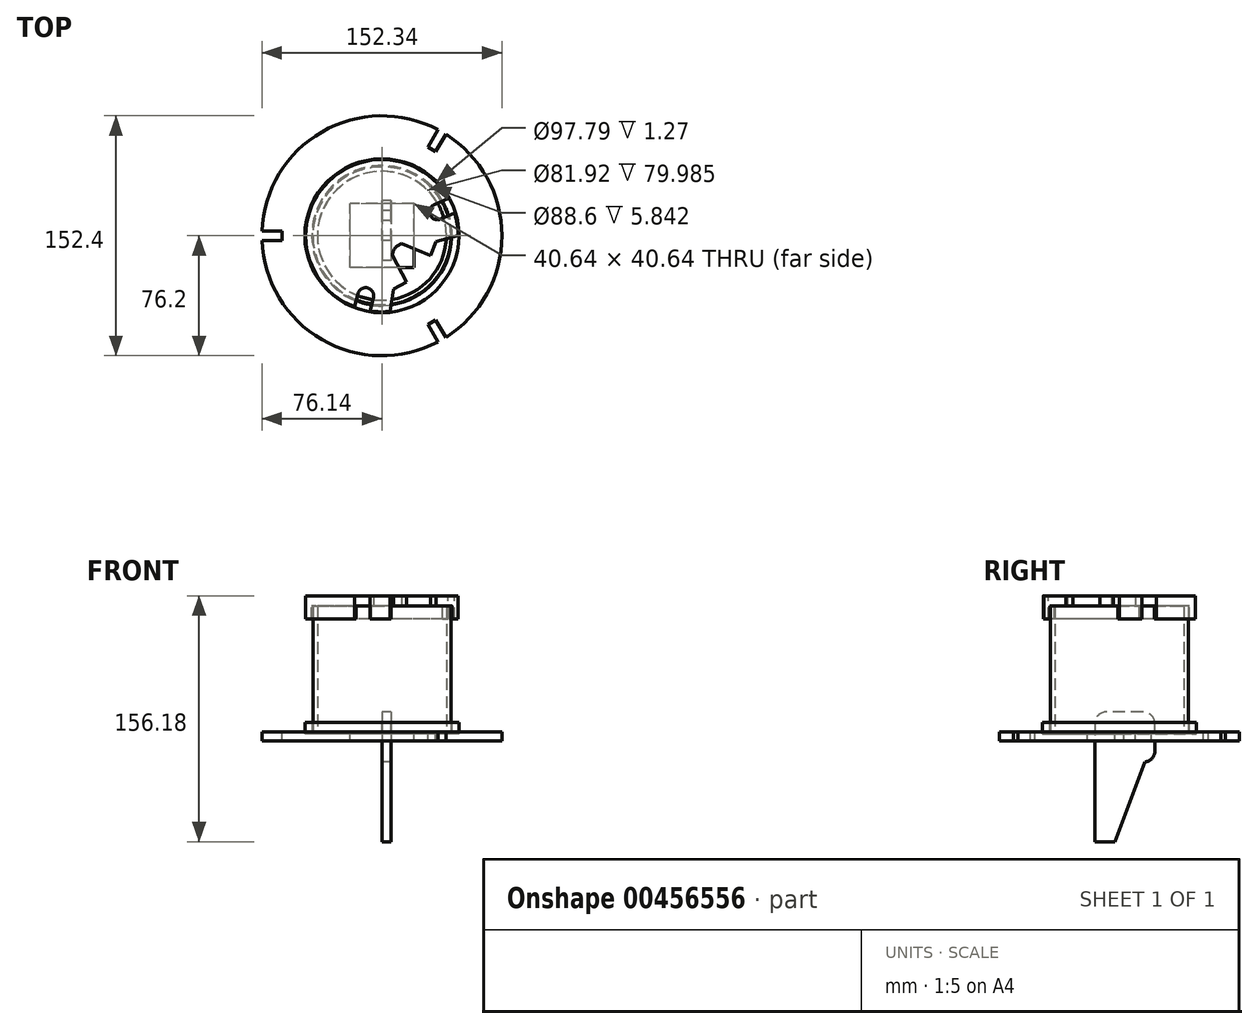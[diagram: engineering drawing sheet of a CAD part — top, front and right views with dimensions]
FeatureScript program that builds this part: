
annotation { "Feature Type Name" : "Feature", "Feature Type Description" : "" }
export const myFeature = defineFeature(function(context is Context, id is Id, definition is map)
    precondition{}
    {
        {
            var Q0;
            Q0=qCreatedBy(makeId("Top.planeOp"),FACE);
            var sketch = newSketch(context, id + "F0", { "sketchPlane" : qUnion([Q0])});
            skCircle(sketch, "E0", {"center": v(0, 0) * mm, "radius": 44.3 * mm});
            skCircle(sketch, "E1", {"center": v(0, 0) * mm, "radius": 40.96 * mm});
            skCircle(sketch, "E2", {"center": v(0, 0) * mm, "radius": 48.9 * mm});
            skCircle(sketch, "E3", {"center": v(0, 0) * mm, "radius": 43.82 * mm});
            skSolve(sketch);
        }
        {
            var Q0;
            Q0=makeQuery(id+"F0.imprint","IMPRINT",FACE,{"disambiguationData":[TD([[makeQuery(id+"F0.imprint","IMPRINT",EDGE,{"derivedFrom":sQuery(id+"F0.wireOp",EDGE,"E1")}),-1.0]])]});
            extrude(context, id + "F1", {"entities" : qUnion([Q0]), "depth" : 79.98 * mm});
        }
        {
            var Q0;
            Q0=qCreatedBy(makeId("Top.planeOp"),FACE);
            var sketch = newSketch(context, id + "F2", { "sketchPlane" : qUnion([Q0])});
            skArc(sketch, "E4", {"start": v(-76.14, -2.92) * mm, "mid": v(-38.1, -66) * mm, "end": v(35.54, -67.4) * mm});
            skLineSegment(sketch, "E5", {"start": v(-76.14, 2.92) * mm, "end": v(-63.44, 2.92) * mm});
            skLineSegment(sketch, "E6", {"start": v(-63.44, 2.92) * mm, "end": v(-63.44, -2.92) * mm});
            skLineSegment(sketch, "E7", {"start": v(-63.44, -2.92) * mm, "end": v(-76.14, -2.92) * mm});
            skLineSegment(sketch, "E8", {"start": v(-63.44, 0) * mm, "end": v(0, 0) * mm, "construction": true});
            skLineSegment(sketch, "E9.bottom", {"start": v(20.32, -20.32) * mm, "end": v(-20.32, -20.32) * mm});
            skLineSegment(sketch, "E9.top", {"start": v(20.32, 20.32) * mm, "end": v(-20.32, 20.32) * mm});
            skLineSegment(sketch, "E9.left", {"start": v(20.32, -20.32) * mm, "end": v(20.32, 20.32) * mm});
            skLineSegment(sketch, "E9.right", {"start": v(-20.32, -20.32) * mm, "end": v(-20.32, 20.32) * mm});
            skLineSegment(sketch, "E10.1.1", {"start": v(34.25, 53.48) * mm, "end": v(29.2, 56.4) * mm});
            skLineSegment(sketch, "E10.1.2", {"start": v(29.2, 56.4) * mm, "end": v(35.54, 67.4) * mm});
            skLineSegment(sketch, "E10.1.3", {"start": v(40.6, 64.48) * mm, "end": v(34.25, 53.48) * mm});
            skLineSegment(sketch, "E10.2.1", {"start": v(29.2, -56.4) * mm, "end": v(34.25, -53.48) * mm});
            skLineSegment(sketch, "E10.2.2", {"start": v(34.25, -53.48) * mm, "end": v(40.6, -64.48) * mm});
            skLineSegment(sketch, "E10.2.3", {"start": v(35.54, -67.4) * mm, "end": v(29.2, -56.4) * mm});
            skLineSegment(sketch, "E10.anchor1", {"start": v(0, 0) * mm, "end": v(-63.44, -2.92) * mm, "construction": true});
            skLineSegment(sketch, "E10.anchor2", {"start": v(0, 0) * mm, "end": v(34.25, -53.48) * mm, "construction": true});
            skArc(sketch, "E11.trimOffspring", {"start": v(40.6, -64.48) * mm, "mid": v(76.2, 0) * mm, "end": v(40.6, 64.48) * mm});
            skArc(sketch, "E12.trimOffspring", {"start": v(35.54, 67.4) * mm, "mid": v(-38.1, 66) * mm, "end": v(-76.14, 2.92) * mm});
            skSolve(sketch);
        }
        {
            var Q0;
            Q0=makeQuery(id+"F2.imprint","IMPRINT",FACE,{"disambiguationData":[TD([[makeQuery(id+"F2.imprint","IMPRINT",EDGE,{"derivedFrom":sQuery(id+"F2.wireOp",EDGE,"E4")}),1.0]])]});
            extrude(context, id + "F3", {"entities" : qUnion([Q0]), "oppositeDirection" : true, "depth" : 5.84 * mm});
        }
        {
            var Q0;
            Q0=makeQuery(id+"F2.imprint","IMPRINT",FACE,{"disambiguationData":[TD([[makeQuery(id+"F2.imprint","IMPRINT",EDGE,{"derivedFrom":sQuery(id+"F2.wireOp",EDGE,"E9.bottom")}),-1.0]])]});
            var Q1;
            Q1 = qSketchRegion(id + "F7", true);
            extrude(context, id + "F4", {"entities" : qUnion([Q0, Q1]), "operationType" : NewBodyOperationType.REMOVE, "endBound" : BoundingType.THROUGH_ALL, "oppositeDirection" : true, "depth" : 25.4 * mm});
        }
        {
            var Q0;
            Q0=qCreatedBy(makeId("Right.planeOp"),FACE);
            var sketch = newSketch(context, id + "F5", { "sketchPlane" : qUnion([Q0])});
            skLineSegment(sketch, "E13", {"start": v(-2.92, 0) * mm, "end": v(-2.92, -69.85) * mm, "construction": true});
            skLineSegment(sketch, "E14", {"start": v(-2.92, -69.85) * mm, "end": v(-15.62, -69.85) * mm});
            skLineSegment(sketch, "E15", {"start": v(-2.92, -69.85) * mm, "end": v(22.48, -69.85) * mm, "construction": true});
            skLineSegment(sketch, "E16", {"start": v(22.48, 0) * mm, "end": v(22.48, 5.08) * mm});
            skLineSegment(sketch, "E17", {"start": v(14.86, 12.7) * mm, "end": v(-8, 12.7) * mm});
            skLineSegment(sketch, "E18", {"start": v(-15.62, 5.08) * mm, "end": v(-15.62, -69.85) * mm});
            skPoint(sketch, "E19.visualSharp", {"position": v(22.48, 12.7) * mm});
            skArc(sketch, "E19.filletArc", {"start": v(22.48, 5.08) * mm, "mid": v(20.25, 10.47) * mm, "end": v(14.86, 12.7) * mm});
            skPoint(sketch, "E20.visualSharp", {"position": v(-15.62, 12.7) * mm});
            skArc(sketch, "E20.filletArc", {"start": v(-8, 12.7) * mm, "mid": v(-13.39, 10.47) * mm, "end": v(-15.62, 5.08) * mm});
            skLineSegment(sketch, "E21", {"start": v(22.48, 0) * mm, "end": v(9.78, 0) * mm});
            skLineSegment(sketch, "E22", {"start": v(9.78, 0) * mm, "end": v(9.78, -5.66) * mm});
            skLineSegment(sketch, "E23", {"start": v(9.78, -5.66) * mm, "end": v(22.48, -5.66) * mm});
            skLineSegment(sketch, "E24", {"start": v(22.48, -5.66) * mm, "end": v(22.48, -12.7) * mm});
            skLineSegment(sketch, "E25", {"start": v(22.48, -18.36) * mm, "end": v(22.48, -69.85) * mm, "construction": true});
            skPoint(sketch, "E26.visualSharp", {"position": v(22.48, -18.36) * mm});
            skArc(sketch, "E26.filletArc", {"start": v(16.13, -19.06) * mm, "mid": v(20.62, -17.2) * mm, "end": v(22.48, -12.7) * mm});
            skLineSegment(sketch, "E27", {"start": v(-2.92, -69.85) * mm, "end": v(16.13, -19.06) * mm});
            skSolve(sketch);
        }
        {
            var Q0;
            Q0=makeQuery(id+"F5.imprint","IMPRINT",FACE,{"disambiguationData":[TD([[makeQuery(id+"F5.imprint","IMPRINT",EDGE,{"derivedFrom":sQuery(id+"F5.wireOp",EDGE,"E14")}),-1.0]])]});
            extrude(context, id + "F6", {"entities" : qUnion([Q0]), "depth" : 5.84 * mm});
        }
        {
            var Q0;
            Q0=makeQuery(id+"F1.opExtrude","CAP_FACE",FACE,{"disambiguationData":[OSD([sQuery(id+"F0.wireOp",EDGE,"E0"),sQuery(id+"F0.wireOp",EDGE,"E1")])],"isStart":false});
            var sketch = newSketch(context, id + "F7", { "sketchPlane" : qUnion([Q0])});
            skArc(sketch, "E28", {"start": v(44.54, -1.06) * mm, "mid": v(44.15, 5.94) * mm, "end": v(42.68, 12.8) * mm});
            skArc(sketch, "E29", {"start": v(48.36, 0) * mm, "mid": v(47.82, 7.23) * mm, "end": v(46.2, 14.3) * mm});
            skLineSegment(sketch, "E30", {"start": v(10.01, -39.72) * mm, "end": v(40.56, -5.7) * mm, "construction": true});
            skLineSegment(sketch, "E31", {"start": v(5.18, -48.08) * mm, "end": v(10.01, -39.72) * mm, "construction": true});
            skLineSegment(sketch, "E32", {"start": v(40.56, -5.7) * mm, "end": v(48.36, 0) * mm, "construction": true});
            skLineSegment(sketch, "E33", {"start": v(40.56, -5.7) * mm, "end": v(34.49, -3.83) * mm, "construction": true});
            skLineSegment(sketch, "E34", {"start": v(10.01, -39.72) * mm, "end": v(7.5, -33.88) * mm, "construction": true});
            skLineSegment(sketch, "E35", {"start": v(7.5, -33.88) * mm, "end": v(34.49, -3.83) * mm, "construction": true});
            skLineSegment(sketch, "E36", {"start": v(34.49, -3.83) * mm, "end": v(48.36, 0) * mm});
            skLineSegment(sketch, "E37", {"start": v(7.5, -33.88) * mm, "end": v(5.18, -48.08) * mm});
            skPoint(sketch, "E38.orphan", {"position": v(7.6, -43.9) * mm});
            skPoint(sketch, "E39.orphan", {"position": v(44.46, -2.85) * mm});
            skLineSegment(sketch, "E40", {"start": v(0, 0) * mm, "end": v(38, -15.3) * mm, "construction": true});
            skLineSegment(sketch, "E41", {"start": v(0, 0) * mm, "end": v(19.28, -36.14) * mm, "construction": true});
            skLineSegment(sketch, "E42", {"start": v(10.01, -39.72) * mm, "end": v(19.28, -36.14) * mm, "construction": true});
            skLineSegment(sketch, "E43", {"start": v(40.56, -5.7) * mm, "end": v(38, -15.3) * mm, "construction": true});
            skLineSegment(sketch, "E44", {"start": v(8.51, -7.65) * mm, "end": v(-30.47, 27.37) * mm, "construction": true});
            skPoint(sketch, "E44.startSnap0", {"position": v(19, -7.65) * mm});
            skLineSegment(sketch, "E45", {"start": v(8.51, -7.65) * mm, "end": v(38, -15.3) * mm, "construction": true});
            skLineSegment(sketch, "E46", {"start": v(8.51, -7.65) * mm, "end": v(19.28, -36.14) * mm, "construction": true});
            skArc(sketch, "E47", {"start": v(12.54, -5.05) * mm, "mid": v(8.4, -7.8) * mm, "end": v(6.64, -12.45) * mm});
            skLineSegment(sketch, "E48", {"start": v(6.64, -12.45) * mm, "end": v(15.7, -29.41) * mm});
            skLineSegment(sketch, "E49", {"start": v(15.7, -29.41) * mm, "end": v(7.5, -33.88) * mm});
            skLineSegment(sketch, "E50", {"start": v(12.54, -5.05) * mm, "end": v(30.93, -12.45) * mm});
            skLineSegment(sketch, "E51", {"start": v(30.93, -12.45) * mm, "end": v(34.49, -3.83) * mm});
            skArc(sketch, "E52", {"start": v(-5.38, -39.33) * mm, "mid": v(-8.96, -33.1) * mm, "end": v(-15.19, -36.68) * mm});
            skPoint(sketch, "E53", {"position": v(-8.96, -33.1) * mm});
            skLineSegment(sketch, "E54", {"start": v(-15.19, -36.68) * mm, "end": v(-16.46, -41.4) * mm});
            skLineSegment(sketch, "E55", {"start": v(-5.38, -39.33) * mm, "end": v(-6.65, -44.05) * mm});
            skLineSegment(sketch, "E56", {"start": v(-16.46, -41.4) * mm, "end": v(-17.46, -45.1) * mm});
            skLineSegment(sketch, "E57", {"start": v(-6.65, -44.05) * mm, "end": v(-7.66, -47.75) * mm});
            skArc(sketch, "E58.trimOffspring", {"start": v(-6.65, -44.05) * mm, "mid": v(-0.42, -44.55) * mm, "end": v(5.82, -44.17) * mm});
            skArc(sketch, "E59.trimOffspring", {"start": v(-7.66, -47.75) * mm, "mid": v(-1.25, -48.35) * mm, "end": v(5.18, -48.08) * mm});
            skPoint(sketch, "E60", {"position": v(-5.7, -40.56) * mm});
            skPoint(sketch, "E61", {"position": v(6.43, -40.45) * mm});
            skArc(sketch, "E62", {"start": v(33.4, 19.87) * mm, "mid": v(30.74, 13.2) * mm, "end": v(37.41, 10.53) * mm});
            skPoint(sketch, "E63", {"position": v(30.74, 13.2) * mm});
            skLineSegment(sketch, "E64", {"start": v(37.41, 10.53) * mm, "end": v(42.68, 12.8) * mm});
            skLineSegment(sketch, "E65", {"start": v(33.4, 19.87) * mm, "end": v(38.67, 22.13) * mm});
            skLineSegment(sketch, "E66", {"start": v(42.68, 12.8) * mm, "end": v(46.2, 14.3) * mm});
            skLineSegment(sketch, "E67", {"start": v(38.67, 22.13) * mm, "end": v(42.2, 23.64) * mm});
            skPoint(sketch, "E68", {"position": v(39.35, 11.36) * mm});
            skPoint(sketch, "E69", {"position": v(40.9, -2.06) * mm});
            skArc(sketch, "E70.trimOffspring", {"start": v(38.67, 22.13) * mm, "mid": v(-33.65, 29.2) * mm, "end": v(-16.46, -41.4) * mm});
            skArc(sketch, "E71.trimOffspring", {"start": v(42.2, 23.64) * mm, "mid": v(-36.53, 31.7) * mm, "end": v(-17.46, -45.1) * mm});
            skSolve(sketch);
        }
        {
            var Q0;
            {var subQ0=sQuery(id+"F7.wireOp",EDGE,"E28");Q0=makeQuery(id+"F7.imprint","IMPRINT",FACE,{"disambiguationData":[TD([[makeQuery(id+"F7.imprint","IMPRINT",EDGE,{"derivedFrom":subQ0}),-1.0]])]});}
            var Q1;
            Q1=makeQuery(id+"F7.imprint","IMPRINT",FACE,{"disambiguationData":[TD([[makeQuery(id+"F7.imprint","IMPRINT",EDGE,{"derivedFrom":sQuery(id+"F7.wireOp",EDGE,"E57")}),1.0]])]});
            var Q2;
            Q2=makeQuery(id+"F7.imprint","IMPRINT",FACE,{"disambiguationData":[TD([[makeQuery(id+"F7.imprint","IMPRINT",EDGE,{"derivedFrom":sQuery(id+"F7.wireOp",EDGE,"E56")}),-1.0]])]});
            extrude(context, id + "F8", {"entities" : qUnion([Q0, Q1, Q2]), "oppositeDirection" : true, "depth" : 8.38 * mm, "offsetDistance" : 25.4 * mm});
        }
        {
            var Q0;
            Q0 = qSketchRegion(id + "F7", true);
            extrude(context, id + "F9", {"entities" : qUnion([Q0]), "operationType" : NewBodyOperationType.ADD, "depth" : 6.35 * mm, "offsetDistance" : 25.4 * mm});
        }
        {
            var Q0;
            Q0 = qSketchRegion(id + "F0", true);
            extrude(context, id + "F10", {"entities" : qUnion([Q0]), "depth" : 5.84 * mm});
        }
        {
            var Q0;
            Q0=makeQuery(id+"F0.imprint","IMPRINT",FACE,{"disambiguationData":[TD([[makeQuery(id+"F0.imprint","IMPRINT",EDGE,{"derivedFrom":sQuery(id+"F0.wireOp",EDGE,"E0")}),-1.0]])]});
            extrude(context, id + "F11", {"entities" : qUnion([Q0]), "operationType" : NewBodyOperationType.REMOVE, "oppositeDirection" : true, "depth" : 1.27 * mm});
        }
    });
